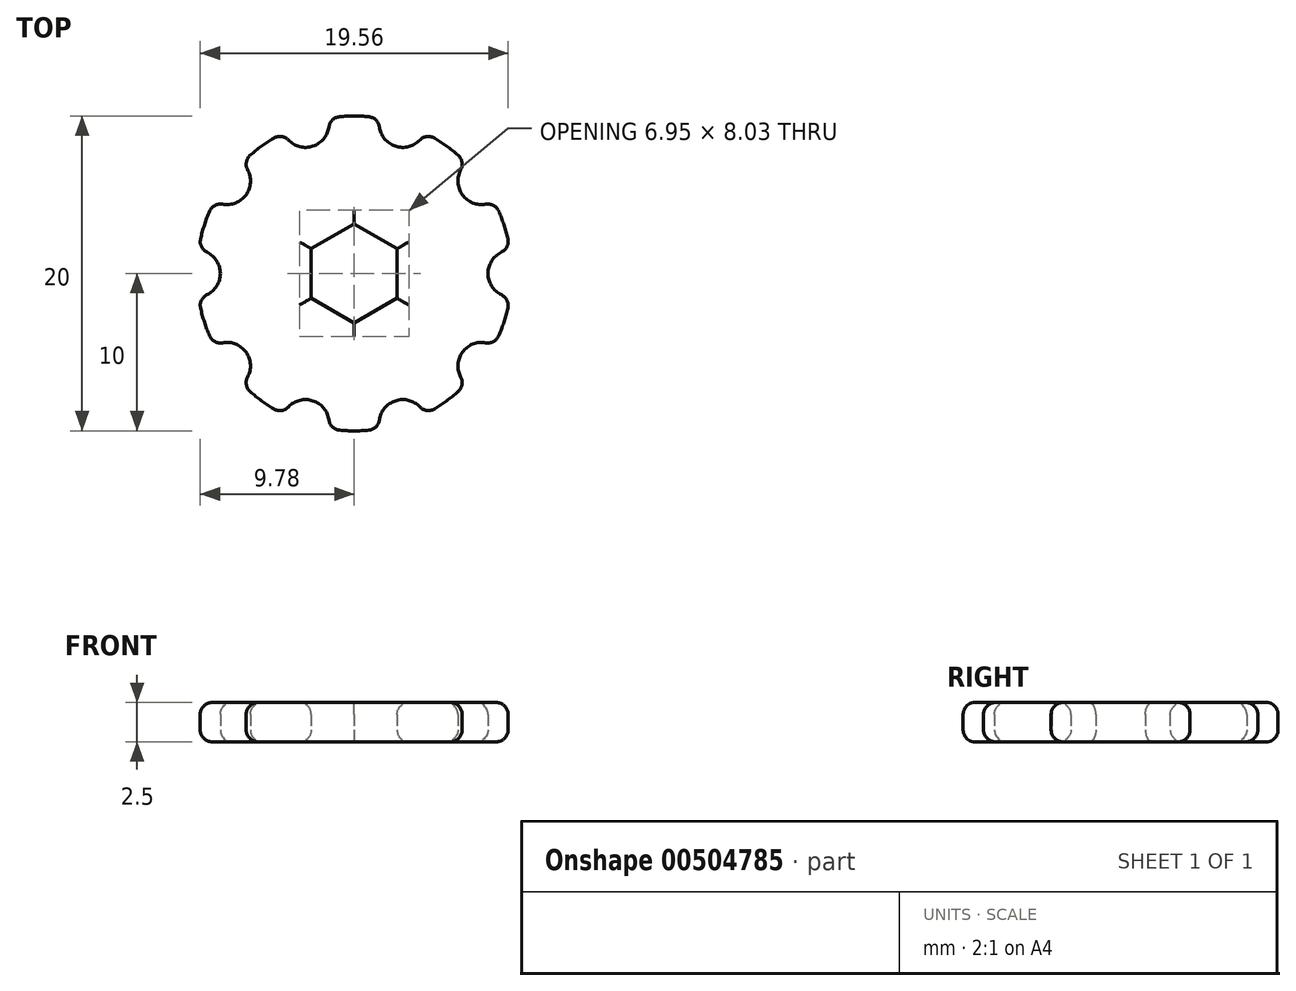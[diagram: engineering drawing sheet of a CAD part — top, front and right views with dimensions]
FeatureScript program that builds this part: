
annotation { "Feature Type Name" : "Feature", "Feature Type Description" : "" }
export const myFeature = defineFeature(function(context is Context, id is Id, definition is map)
    precondition{}
    {
        {
            var Q0;
            Q0=qCreatedBy(makeId("Top.planeOp"),FACE);
            var sketch = newSketch(context, id + "F0", { "sketchPlane" : qUnion([Q0])});
            skCircle(sketch, "E0.cCircle", {"center": v(0, 0) * mm, "radius": 2.73 * mm, "construction": true});
            skLineSegment(sketch, "E0.0", {"start": v(2.73, 1.57) * mm, "end": v(2.73, -1.57) * mm});
            skLineSegment(sketch, "E0.1", {"start": v(2.73, -1.57) * mm, "end": v(0, -3.15) * mm});
            skLineSegment(sketch, "E0.2", {"start": v(0, -3.15) * mm, "end": v(-2.73, -1.57) * mm});
            skLineSegment(sketch, "E0.3", {"start": v(-2.72, -1.57) * mm, "end": v(-2.73, 1.57) * mm});
            skLineSegment(sketch, "E0.4", {"start": v(-2.73, 1.57) * mm, "end": v(0, 3.15) * mm});
            skLineSegment(sketch, "E0.5", {"start": v(0, 3.15) * mm, "end": v(2.73, 1.57) * mm});
            skPoint(sketch, "E0.0.midPoint", {"position": v(2.73, 0) * mm});
            skCircle(sketch, "E1", {"center": v(0, 0) * mm, "radius": 10 * mm});
            skCircle(sketch, "E2", {"center": v(10, 0) * mm, "radius": 1.5 * mm});
            skCircle(sketch, "E3.1.0", {"center": v(8.1, 5.88) * mm, "radius": 1.5 * mm});
            skCircle(sketch, "E3.2.0", {"center": v(3.1, 9.51) * mm, "radius": 1.5 * mm});
            skCircle(sketch, "E3.3.0", {"center": v(-3.1, 9.51) * mm, "radius": 1.5 * mm});
            skCircle(sketch, "E3.4.0", {"center": v(-8.1, 5.88) * mm, "radius": 1.5 * mm});
            skCircle(sketch, "E3.5.0", {"center": v(-10, 0) * mm, "radius": 1.5 * mm});
            skCircle(sketch, "E3.6.0", {"center": v(-8.1, -5.88) * mm, "radius": 1.5 * mm});
            skCircle(sketch, "E3.7.0", {"center": v(-3.1, -9.51) * mm, "radius": 1.5 * mm});
            skCircle(sketch, "E3.8.0", {"center": v(3.1, -9.51) * mm, "radius": 1.5 * mm});
            skCircle(sketch, "E3.9.0", {"center": v(8.1, -5.88) * mm, "radius": 1.5 * mm});
            skSolve(sketch);
        }
        {
            var Q0;
            Q0=makeQuery(id+"F0.imprint","IMPRINT",FACE,{"disambiguationData":[TD([[makeQuery(id+"F0.imprint","IMPRINT",EDGE,{"derivedFrom":sQuery(id+"F0.wireOp",EDGE,"E0.0")}),1.0]])]});
            extrude(context, id + "F1", {"entities" : qUnion([Q0]), "depth" : 2.5 * mm});
        }
        {
            var Q0;
            Q0=makeQuery(id+"F1.opExtrude","CAP_FACE",FACE,{"disambiguationData":[OSD([sQuery(id+"F0.wireOp",EDGE,"E0.0"),sQuery(id+"F0.wireOp",EDGE,"E0.1"),sQuery(id+"F0.wireOp",EDGE,"E0.2"),sQuery(id+"F0.wireOp",EDGE,"E0.3"),sQuery(id+"F0.wireOp",EDGE,"E0.4"),sQuery(id+"F0.wireOp",EDGE,"E0.5"),sQuery(id+"F0.wireOp",EDGE,"E1"),sQuery(id+"F0.wireOp",EDGE,"E2"),sQuery(id+"F0.wireOp",EDGE,"E3.1.0"),sQuery(id+"F0.wireOp",EDGE,"E3.2.0"),sQuery(id+"F0.wireOp",EDGE,"E3.3.0"),sQuery(id+"F0.wireOp",EDGE,"E3.4.0"),sQuery(id+"F0.wireOp",EDGE,"E3.5.0"),sQuery(id+"F0.wireOp",EDGE,"E3.6.0"),sQuery(id+"F0.wireOp",EDGE,"E3.7.0"),sQuery(id+"F0.wireOp",EDGE,"E3.8.0"),sQuery(id+"F0.wireOp",EDGE,"E3.9.0")])],"isStart":false});
            var Q1;
            Q1=makeQuery(id+"F1.opExtrude","CAP_FACE",FACE,{"disambiguationData":[OSD([sQuery(id+"F0.wireOp",EDGE,"E0.0"),sQuery(id+"F0.wireOp",EDGE,"E0.1"),sQuery(id+"F0.wireOp",EDGE,"E0.2"),sQuery(id+"F0.wireOp",EDGE,"E0.3"),sQuery(id+"F0.wireOp",EDGE,"E0.4"),sQuery(id+"F0.wireOp",EDGE,"E0.5"),sQuery(id+"F0.wireOp",EDGE,"E1"),sQuery(id+"F0.wireOp",EDGE,"E2"),sQuery(id+"F0.wireOp",EDGE,"E3.1.0"),sQuery(id+"F0.wireOp",EDGE,"E3.2.0"),sQuery(id+"F0.wireOp",EDGE,"E3.3.0"),sQuery(id+"F0.wireOp",EDGE,"E3.4.0"),sQuery(id+"F0.wireOp",EDGE,"E3.5.0"),sQuery(id+"F0.wireOp",EDGE,"E3.6.0"),sQuery(id+"F0.wireOp",EDGE,"E3.7.0"),sQuery(id+"F0.wireOp",EDGE,"E3.8.0"),sQuery(id+"F0.wireOp",EDGE,"E3.9.0")])],"isStart":true});
            var Q2;
            {var subQ0=sQuery(id+"F0.wireOp",EDGE,"E3.7.0");var subQ1=sQuery(id+"F0.wireOp",EDGE,"E1");Q2=makeQuery(id+"F1.opExtrude","SWEPT_EDGE",EDGE,{"disambiguationData":[OSD([subQ1,subQ0]),TDD([makeQuery(id+"F0.imprint","INTERSECT",VERTEX,{"disambiguationData":[OD(0.0)],"derivedFrom":[subQ1,subQ0]})])]});}
            var Q3;
            {var subQ0=sQuery(id+"F0.wireOp",EDGE,"E3.7.0");var subQ1=sQuery(id+"F0.wireOp",EDGE,"E1");Q3=makeQuery(id+"F1.opExtrude","SWEPT_EDGE",EDGE,{"disambiguationData":[OSD([subQ1,subQ0]),TDD([makeQuery(id+"F0.imprint","INTERSECT",VERTEX,{"disambiguationData":[OD(1.0)],"derivedFrom":[subQ1,subQ0]})])]});}
            var Q4;
            {var subQ0=sQuery(id+"F0.wireOp",EDGE,"E3.8.0");var subQ1=sQuery(id+"F0.wireOp",EDGE,"E1");Q4=makeQuery(id+"F1.opExtrude","SWEPT_EDGE",EDGE,{"disambiguationData":[OSD([subQ1,subQ0]),TDD([makeQuery(id+"F0.imprint","INTERSECT",VERTEX,{"disambiguationData":[OD(0.0)],"derivedFrom":[subQ1,subQ0]})])]});}
            var Q5;
            {var subQ0=sQuery(id+"F0.wireOp",EDGE,"E3.8.0");var subQ1=sQuery(id+"F0.wireOp",EDGE,"E1");Q5=makeQuery(id+"F1.opExtrude","SWEPT_EDGE",EDGE,{"disambiguationData":[OSD([subQ1,subQ0]),TDD([makeQuery(id+"F0.imprint","INTERSECT",VERTEX,{"disambiguationData":[OD(1.0)],"derivedFrom":[subQ1,subQ0]})])]});}
            var Q6;
            {var subQ0=sQuery(id+"F0.wireOp",EDGE,"E3.9.0");var subQ1=sQuery(id+"F0.wireOp",EDGE,"E1");Q6=makeQuery(id+"F1.opExtrude","SWEPT_EDGE",EDGE,{"disambiguationData":[OSD([subQ1,subQ0]),TDD([makeQuery(id+"F0.imprint","INTERSECT",VERTEX,{"disambiguationData":[OD(0.0)],"derivedFrom":[subQ1,subQ0]})])]});}
            var Q7;
            {var subQ0=sQuery(id+"F0.wireOp",EDGE,"E3.9.0");var subQ1=sQuery(id+"F0.wireOp",EDGE,"E1");Q7=makeQuery(id+"F1.opExtrude","SWEPT_EDGE",EDGE,{"disambiguationData":[OSD([subQ1,subQ0]),TDD([makeQuery(id+"F0.imprint","INTERSECT",VERTEX,{"disambiguationData":[OD(1.0)],"derivedFrom":[subQ1,subQ0]})])]});}
            var Q8;
            {var subQ0=sQuery(id+"F0.wireOp",EDGE,"E2");var subQ1=sQuery(id+"F0.wireOp",EDGE,"E1");Q8=makeQuery(id+"F1.opExtrude","SWEPT_EDGE",EDGE,{"disambiguationData":[OSD([subQ1,subQ0]),TDD([makeQuery(id+"F0.imprint","INTERSECT",VERTEX,{"disambiguationData":[OD(1.0)],"derivedFrom":[subQ1,subQ0]})])]});}
            var Q9;
            {var subQ0=sQuery(id+"F0.wireOp",EDGE,"E2");var subQ1=sQuery(id+"F0.wireOp",EDGE,"E1");Q9=makeQuery(id+"F1.opExtrude","SWEPT_EDGE",EDGE,{"disambiguationData":[OSD([subQ1,subQ0]),TDD([makeQuery(id+"F0.imprint","INTERSECT",VERTEX,{"disambiguationData":[OD(0.0)],"derivedFrom":[subQ1,subQ0]})])]});}
            var Q10;
            {var subQ0=sQuery(id+"F0.wireOp",EDGE,"E3.1.0");var subQ1=sQuery(id+"F0.wireOp",EDGE,"E1");Q10=makeQuery(id+"F1.opExtrude","SWEPT_EDGE",EDGE,{"disambiguationData":[OSD([subQ1,subQ0]),TDD([makeQuery(id+"F0.imprint","INTERSECT",VERTEX,{"disambiguationData":[OD(0.0)],"derivedFrom":[subQ1,subQ0]})])]});}
            var Q11;
            {var subQ0=sQuery(id+"F0.wireOp",EDGE,"E3.1.0");var subQ1=sQuery(id+"F0.wireOp",EDGE,"E1");Q11=makeQuery(id+"F1.opExtrude","SWEPT_EDGE",EDGE,{"disambiguationData":[OSD([subQ1,subQ0]),TDD([makeQuery(id+"F0.imprint","INTERSECT",VERTEX,{"disambiguationData":[OD(1.0)],"derivedFrom":[subQ1,subQ0]})])]});}
            var Q12;
            {var subQ0=sQuery(id+"F0.wireOp",EDGE,"E3.2.0");var subQ1=sQuery(id+"F0.wireOp",EDGE,"E1");Q12=makeQuery(id+"F1.opExtrude","SWEPT_EDGE",EDGE,{"disambiguationData":[OSD([subQ1,subQ0]),TDD([makeQuery(id+"F0.imprint","INTERSECT",VERTEX,{"disambiguationData":[OD(0.0)],"derivedFrom":[subQ1,subQ0]})])]});}
            var Q13;
            {var subQ0=sQuery(id+"F0.wireOp",EDGE,"E3.2.0");var subQ1=sQuery(id+"F0.wireOp",EDGE,"E1");Q13=makeQuery(id+"F1.opExtrude","SWEPT_EDGE",EDGE,{"disambiguationData":[OSD([subQ1,subQ0]),TDD([makeQuery(id+"F0.imprint","INTERSECT",VERTEX,{"disambiguationData":[OD(1.0)],"derivedFrom":[subQ1,subQ0]})])]});}
            var Q14;
            {var subQ0=sQuery(id+"F0.wireOp",EDGE,"E3.3.0");var subQ1=sQuery(id+"F0.wireOp",EDGE,"E1");Q14=makeQuery(id+"F1.opExtrude","SWEPT_EDGE",EDGE,{"disambiguationData":[OSD([subQ1,subQ0]),TDD([makeQuery(id+"F0.imprint","INTERSECT",VERTEX,{"disambiguationData":[OD(0.0)],"derivedFrom":[subQ1,subQ0]})])]});}
            var Q15;
            {var subQ0=sQuery(id+"F0.wireOp",EDGE,"E3.3.0");var subQ1=sQuery(id+"F0.wireOp",EDGE,"E1");Q15=makeQuery(id+"F1.opExtrude","SWEPT_EDGE",EDGE,{"disambiguationData":[OSD([subQ1,subQ0]),TDD([makeQuery(id+"F0.imprint","INTERSECT",VERTEX,{"disambiguationData":[OD(1.0)],"derivedFrom":[subQ1,subQ0]})])]});}
            var Q16;
            {var subQ0=sQuery(id+"F0.wireOp",EDGE,"E3.4.0");var subQ1=sQuery(id+"F0.wireOp",EDGE,"E1");Q16=makeQuery(id+"F1.opExtrude","SWEPT_EDGE",EDGE,{"disambiguationData":[OSD([subQ1,subQ0]),TDD([makeQuery(id+"F0.imprint","INTERSECT",VERTEX,{"disambiguationData":[OD(0.0)],"derivedFrom":[subQ1,subQ0]})])]});}
            var Q17;
            {var subQ0=sQuery(id+"F0.wireOp",EDGE,"E3.4.0");var subQ1=sQuery(id+"F0.wireOp",EDGE,"E1");Q17=makeQuery(id+"F1.opExtrude","SWEPT_EDGE",EDGE,{"disambiguationData":[OSD([subQ1,subQ0]),TDD([makeQuery(id+"F0.imprint","INTERSECT",VERTEX,{"disambiguationData":[OD(1.0)],"derivedFrom":[subQ1,subQ0]})])]});}
            var Q18;
            {var subQ0=sQuery(id+"F0.wireOp",EDGE,"E3.5.0");var subQ1=sQuery(id+"F0.wireOp",EDGE,"E1");Q18=makeQuery(id+"F1.opExtrude","SWEPT_EDGE",EDGE,{"disambiguationData":[OSD([subQ1,subQ0]),TDD([makeQuery(id+"F0.imprint","INTERSECT",VERTEX,{"disambiguationData":[OD(0.0)],"derivedFrom":[subQ1,subQ0]})])]});}
            var Q19;
            {var subQ0=sQuery(id+"F0.wireOp",EDGE,"E3.5.0");var subQ1=sQuery(id+"F0.wireOp",EDGE,"E1");Q19=makeQuery(id+"F1.opExtrude","SWEPT_EDGE",EDGE,{"disambiguationData":[OSD([subQ1,subQ0]),TDD([makeQuery(id+"F0.imprint","INTERSECT",VERTEX,{"disambiguationData":[OD(1.0)],"derivedFrom":[subQ1,subQ0]})])]});}
            var Q20;
            {var subQ0=sQuery(id+"F0.wireOp",EDGE,"E3.6.0");var subQ1=sQuery(id+"F0.wireOp",EDGE,"E1");Q20=makeQuery(id+"F1.opExtrude","SWEPT_EDGE",EDGE,{"disambiguationData":[OSD([subQ1,subQ0]),TDD([makeQuery(id+"F0.imprint","INTERSECT",VERTEX,{"disambiguationData":[OD(0.0)],"derivedFrom":[subQ1,subQ0]})])]});}
            var Q21;
            {var subQ0=sQuery(id+"F0.wireOp",EDGE,"E3.6.0");var subQ1=sQuery(id+"F0.wireOp",EDGE,"E1");Q21=makeQuery(id+"F1.opExtrude","SWEPT_EDGE",EDGE,{"disambiguationData":[OSD([subQ1,subQ0]),TDD([makeQuery(id+"F0.imprint","INTERSECT",VERTEX,{"disambiguationData":[OD(1.0)],"derivedFrom":[subQ1,subQ0]})])]});}
            fillet(context, id + "F2", {"entities" : qUnion([Q0, Q1, Q2, Q3, Q4, Q5, Q6, Q7, Q8, Q9, Q10, Q11, Q12, Q13, Q14, Q15, Q16, Q17, Q18, Q19, Q20, Q21]), "radius" : .75 * mm, "tangentPropagation" : true, "allowEdgeOverflow" : false});
        }
    });
